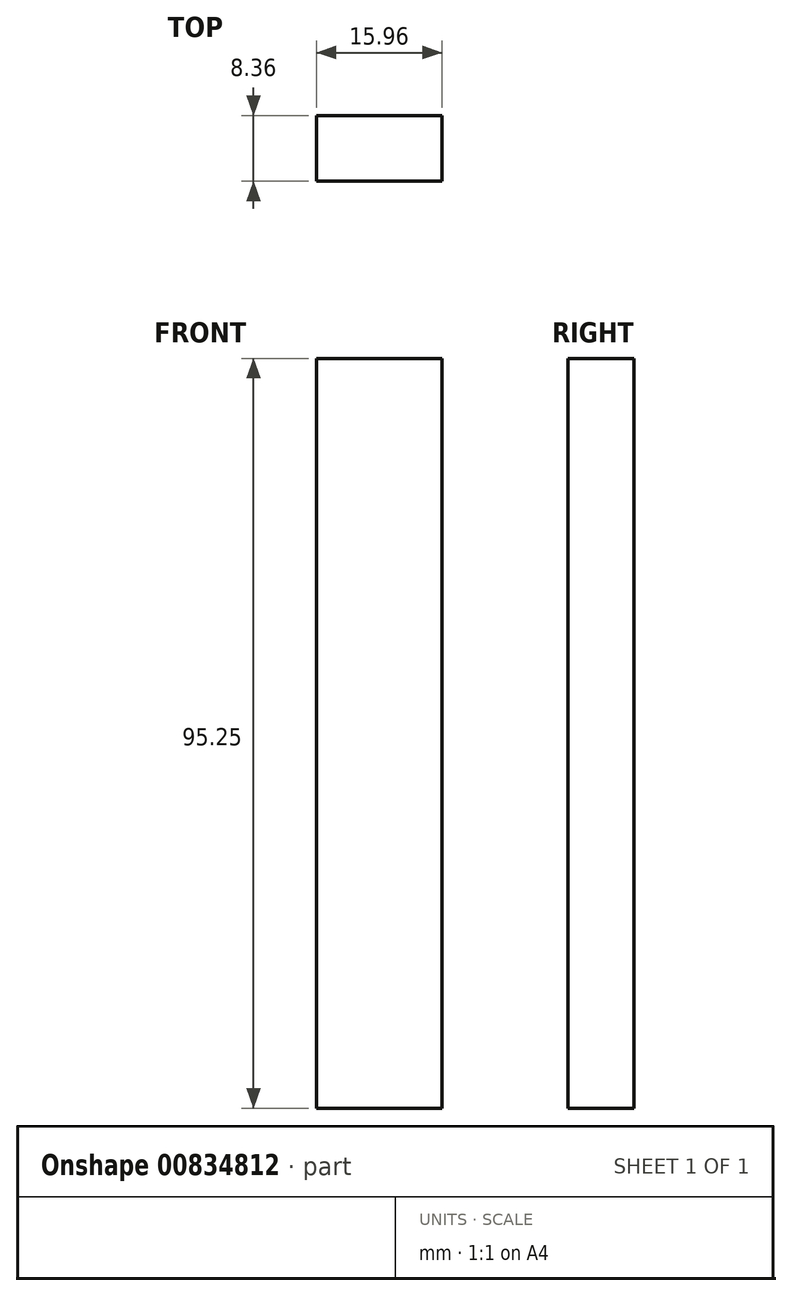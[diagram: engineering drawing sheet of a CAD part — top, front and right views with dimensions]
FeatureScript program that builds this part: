
annotation { "Feature Type Name" : "Feature", "Feature Type Description" : "" }
export const myFeature = defineFeature(function(context is Context, id is Id, definition is map)
    precondition{}
    {
        {
            var Q0;
            Q0=qCreatedBy(makeId("Top.planeOp"),FACE);
            var sketch = newSketch(context, id + "F0", { "sketchPlane" : qUnion([Q0])});
            skLineSegment(sketch, "E0.bottom", {"start": v(0, 0) * mm, "end": v(15.96, 0) * mm});
            skLineSegment(sketch, "E0.top", {"start": v(0, -8.36) * mm, "end": v(15.96, -8.36) * mm});
            skLineSegment(sketch, "E0.left", {"start": v(0, 0) * mm, "end": v(0, -8.36) * mm});
            skLineSegment(sketch, "E0.right", {"start": v(15.96, 0) * mm, "end": v(15.96, -8.36) * mm});
            skSolve(sketch);
        }
        {
            var Q0;
            Q0 = qSketchRegion(id + "F0", true);
            extrude(context, id + "F1", {"entities" : qUnion([Q0]), "depth" : 95.25 * mm, "offsetDistance" : 25.4 * mm});
        }
    });
